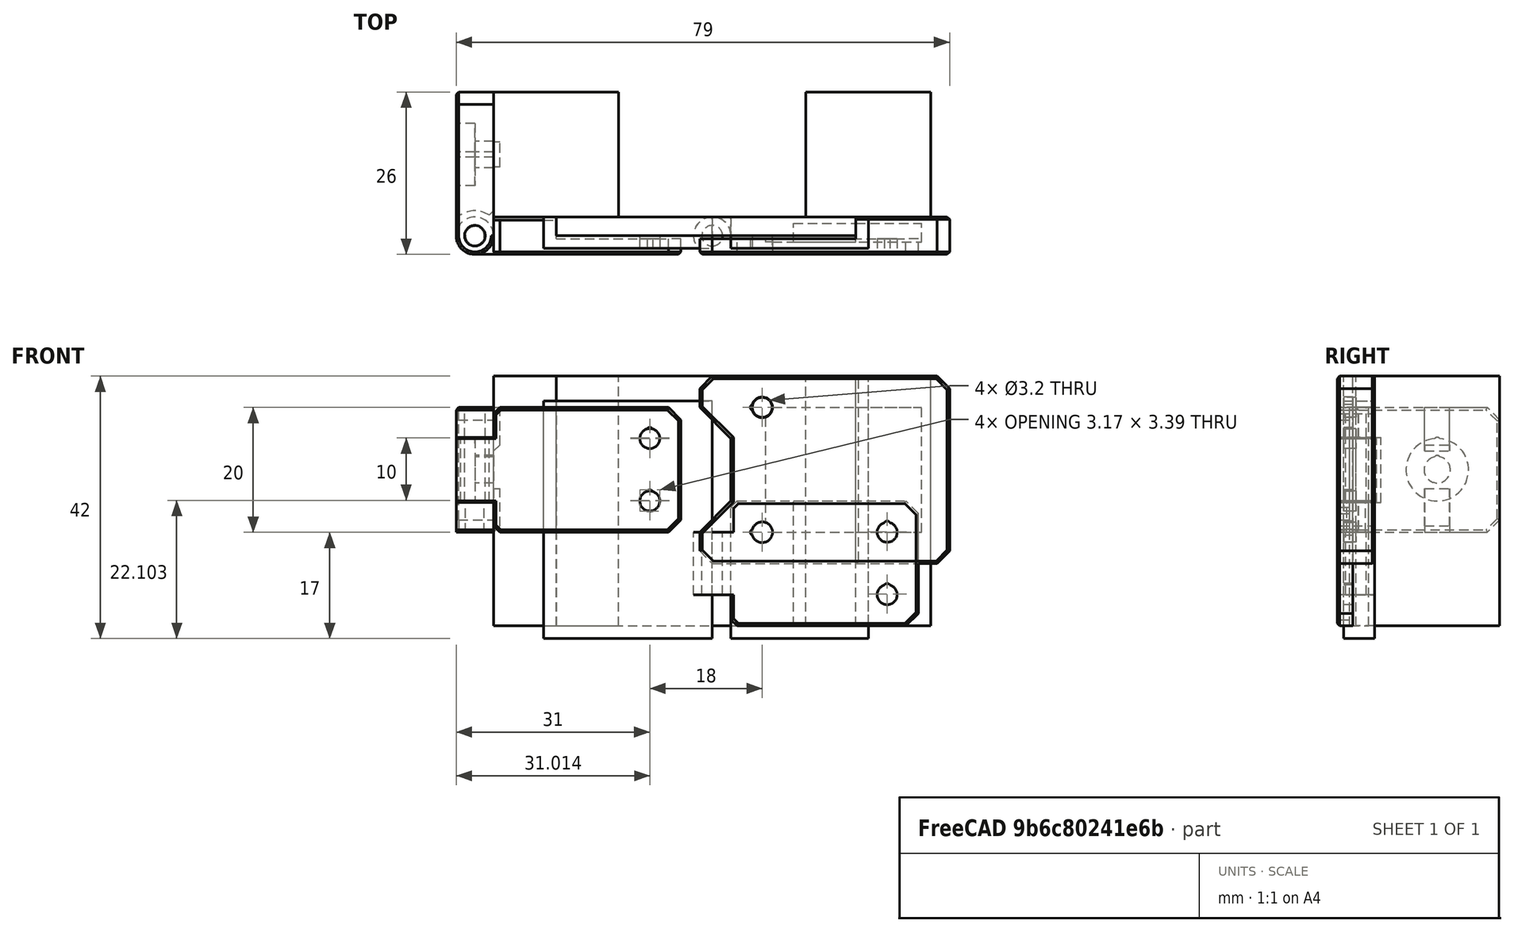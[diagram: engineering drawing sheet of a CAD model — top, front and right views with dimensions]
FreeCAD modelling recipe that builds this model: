
FCSTD DOCUMENT  (FreeCAD 0.18R14555 (Git shallow))
Label: filament-door
License: All rights reserved
LicenseURL: http://en.wikipedia.org/wiki/All_rights_reserved
objects: Part::Cylinder×27, Part::Box×20, Part::Cut×20, Part::Chamfer×14, Part::MultiFuse×13, Part::Feature×2
note: 96 computed .brp shape members not serialized (recipe doc carries the construction recipe); baked Part::Feature solids carry a one-line shape summary decoded from their .brp

FEATURE [Part::Box] Box  label="2020"
  AttacherType = Attacher::AttachEngine3D
  Height = 40
  Length = 20
  Placement = pos=(12,0,0) rot=(0,0,1;0rad)
  Width = 20
FEATURE [Part::Box] Box001  label="acrylic"
  AttacherType = Attacher::AttachEngine3D
  Height = 40
  Length = 48
  Placement = pos=(-28,-3,0) rot=(0,0,1;0rad)
  Width = 3
FEATURE [Part::Cylinder] Cylinder
  Angle = 360
  AttacherType = Attacher::AttachEngine3D
  Height = 10
  Placement = pos=(-3,-3,5) rot=(0,0,1;0rad)
  Radius = 3
FEATURE [Part::Cylinder] Cylinder001
  Angle = 360
  AttacherType = Attacher::AttachEngine3D
  Height = 10
  Placement = pos=(-3,-3,5) rot=(0,0,1;0rad)
  Radius = 1.65
FEATURE [Part::Box] Box005  label="Cube003"
  AttacherType = Attacher::AttachEngine3D
  Height = 20
  Length = 30
  Placement = pos=(0,-6,0) rot=(0,0,1;0rad)
  Width = 3
FEATURE [Part::Box] Box006  label="Cube004"
  AttacherType = Attacher::AttachEngine3D
  Height = 20
  Length = 30
  Placement = pos=(0,-3.5,0) rot=(0,0,1;0rad)
  Width = 3
FEATURE [Part::Box] Box007  label="Cube005"
  AttacherType = Attacher::AttachEngine3D
  Height = 10
  Length = 4
  Placement = pos=(-3,-6,5) rot=(0,0,1;0rad)
  Width = 3
FEATURE [Part::Cylinder] Cylinder002
  Angle = 360
  AttacherType = Attacher::AttachEngine3D
  Height = 10
  Placement = pos=(25,1.1e-15,5) rot=(1,0,0;1.5708rad)
  Radius = 0.5
FEATURE [Part::Cylinder] Cylinder003
  Angle = 360
  AttacherType = Attacher::AttachEngine3D
  Height = 10
  Placement = pos=(25,3e-15,15) rot=(1,0,0;1.5708rad)
  Radius = 0.5
FEATURE [Part::Cylinder] Cylinder004
  Angle = 360
  AttacherType = Attacher::AttachEngine3D
  Height = 10
  Placement = pos=(25,3e-15,15) rot=(1,0,0;1.5708rad)
  Radius = 1.6
FEATURE [Part::Cylinder] Cylinder005
  Angle = 360
  AttacherType = Attacher::AttachEngine3D
  Height = 10
  Placement = pos=(25,1.1e-15,5) rot=(1,0,0;1.5708rad)
  Radius = 1.6
FEATURE [Part::Chamfer] Chamfer
  Base = -> Box005
  Edges = 2 edges r=1: [Edge2,Edge4]
FEATURE [Part::Chamfer] Chamfer001
  Base = -> Chamfer
  Edges = 2 edges r=2: [Edge17,Edge18]
FEATURE [Part::Chamfer] Chamfer002
  Base = -> Chamfer001
  Edges = 8 edges r=0.4: [Edge1,Edge2,Edge3,Edge4,Edge5,Edge6,Edge7,Edge8]
FEATURE [Part::MultiFuse] Fusion
  Shapes = -> [Chamfer002,Box007,Cylinder]
FEATURE [Part::Cut] Cut
  Base = -> Fusion
  Tool = -> Box006
FEATURE [Part::Cut] Cut001
  Base = -> Cut
  Tool = -> Cylinder001
FEATURE [Part::MultiFuse] Fusion001
  Shapes = -> [Cylinder004,Cylinder005]
FEATURE [Part::Cut] Cut002
  Base = -> Cut001
  Tool = -> Fusion001
FEATURE [Part::MultiFuse] Fusion002
  Placement = pos=(0,0,1.3) rot=(0,0,1;0rad)
  Shapes = -> [Cylinder002,Cylinder003]
FEATURE [Part::Cut] Cut003  label="arm"
  Base = -> Cut002
  Placement = pos=(-38,0,15) rot=(0,0,1;0rad)
  Tool = -> Fusion002
FEATURE [Part::Cylinder] Cylinder006
  Angle = 360
  AttacherType = Attacher::AttachEngine3D
  Height = 4.8
  Placement = pos=(-3,-3,0) rot=(0,0,1;0rad)
  Radius = 3
FEATURE [Part::Cylinder] Cylinder007
  Angle = 360
  AttacherType = Attacher::AttachEngine3D
  Height = 4.8
  Placement = pos=(-3,-3,15.2) rot=(0,0,1;0rad)
  Radius = 3
FEATURE [Part::Box] Box008  label="Cube"
  AttacherType = Attacher::AttachEngine3D
  Height = 20
  Length = 6
  Placement = pos=(-6,-3,0) rot=(0,0,1;0rad)
  Width = 23
FEATURE [Part::Box] Box009  label="Cube006"
  AttacherType = Attacher::AttachEngine3D
  Height = 10.4
  Length = 6
  Placement = pos=(-6,-3,4.8) rot=(0,0,1;0rad)
  Width = 3
FEATURE [Part::Cylinder] Cylinder008
  Angle = 360
  AttacherType = Attacher::AttachEngine3D
  Height = 4.8
  Placement = pos=(-3,-3,15.2) rot=(0,0,1;0rad)
  Radius = 1.65
FEATURE [Part::Cylinder] Cylinder009
  Angle = 360
  AttacherType = Attacher::AttachEngine3D
  Height = 4.8
  Placement = pos=(-3,-3,0) rot=(0,0,1;0rad)
  Radius = 1.65
FEATURE [Part::MultiFuse] Fusion004
  Shapes = -> [Cylinder009,Cylinder008]
FEATURE [Part::Chamfer] Chamfer003
  Base = -> Box008
  Edges = 2 edges r=2: [Edge11,Edge12]
FEATURE [Part::Chamfer] Chamfer004
  Base = -> Chamfer003
  Edges = 6 edges r=0.4: [Edge1,Edge2,Edge3,Edge4,Edge5,Edge6]
FEATURE [Part::Chamfer] Chamfer005
  Base = -> Cylinder007
  Edges = 1 edges r=0.4: [Edge1]
FEATURE [Part::Chamfer] Chamfer006
  Base = -> Cylinder006
  Edges = 1 edges r=0.4: [Edge3]
FEATURE [Part::Cut] Cut004
  Base = -> Chamfer004
  Tool = -> Box009
FEATURE [Part::MultiFuse] Fusion005
  Shapes = -> [Cut004,Chamfer005,Chamfer006]
FEATURE [Part::Cut] Cut005
  Base = -> Fusion005
  Tool = -> Fusion004
FEATURE [Part::Chamfer] Chamfer007
  Base = -> Cut005
  Edges = 2 edges r=1: [Edge8,Edge28]
FEATURE [Part::Cylinder] Cylinder010
  Angle = 360
  AttacherType = Attacher::AttachEngine3D
  Height = 10
  Placement = pos=(-2e-15,10,10) rot=(0,-1,0;1.5708rad)
  Radius = 2.1
FEATURE [Part::Cylinder] Cylinder011
  Angle = 360
  AttacherType = Attacher::AttachEngine3D
  Height = 10
  Placement = pos=(-2e-15,10,11.8) rot=(0,-1,0;1.5708rad)
  Radius = 0.5
FEATURE [Part::Cut] Cut006
  Base = -> Chamfer007
  Tool = -> Cylinder010
FEATURE [Part::Cut] Cut007
  Base = -> Cut006
  Tool = -> Cylinder011
FEATURE [Part::Cylinder] Cylinder012
  Angle = 360
  AttacherType = Attacher::AttachEngine3D
  Height = 10
  Placement = pos=(-3,10,14.7) rot=(0,-1,0;1.5708rad)
  Radius = 0.5
FEATURE [Part::Cylinder] Cylinder013
  Angle = 360
  AttacherType = Attacher::AttachEngine3D
  Height = 10
  Placement = pos=(-3,10,10) rot=(0,-1,0;1.5708rad)
  Radius = 5
FEATURE [Part::Cut] Cut008
  Base = -> Cut007
  Tool = -> Cylinder013
FEATURE [Part::Cut] Cut009
  Base = -> Cut008
  Tool = -> Cylinder012
FEATURE [Part::Box] Box010  label="Cube007"
  AttacherType = Attacher::AttachEngine3D
  Height = 7
  Length = 2
  Placement = pos=(-1,8,0) rot=(0,0,1;0rad)
  Width = 4
FEATURE [Part::Box] Box011  label="Cube008"
  AttacherType = Attacher::AttachEngine3D
  Height = 7
  Length = 2
  Placement = pos=(-1,8,13) rot=(0,0,1;0rad)
  Width = 4
FEATURE [Part::Chamfer] Chamfer008
  Base = -> Box011
  Edges = 1 edges r=1: [Edge8]
FEATURE [Part::Chamfer] Chamfer009
  Base = -> Box010
  Edges = 1 edges r=1: [Edge8]
FEATURE [Part::MultiFuse] Fusion006
  Shapes = -> [Chamfer009,Cut009,Chamfer008]
FEATURE [Part::Cylinder] Cylinder014
  Angle = 360
  AttacherType = Attacher::AttachEngine3D
  Height = 4.8
  Placement = pos=(-41,-3,15) rot=(0,0,1;0rad)
  Radius = 3
FEATURE [Part::Cylinder] Cylinder015
  Angle = 360
  AttacherType = Attacher::AttachEngine3D
  Height = 10
  Placement = pos=(-41,-3,20) rot=(0,0,1;0rad)
  Radius = 3
FEATURE [Part::Cylinder] Cylinder016
  Angle = 360
  AttacherType = Attacher::AttachEngine3D
  Height = 10.4
  Placement = pos=(-3,-3,4.8) rot=(0,0,1;0rad)
  Radius = 4
FEATURE [Part::Cut] Cut010
  Base = -> Fusion006
  Tool = -> Cylinder016
FEATURE [Part::Cylinder] Cylinder017
  Angle = 360
  AttacherType = Attacher::AttachEngine3D
  Height = 4.8
  Placement = pos=(-3,-3,0) rot=(0,0,1;0rad)
  Radius = 2
FEATURE [Part::Cylinder] Cylinder018
  Angle = 360
  AttacherType = Attacher::AttachEngine3D
  Height = 4.8
  Placement = pos=(-3,-3,0) rot=(0,0,1;0rad)
  Radius = 1.5
FEATURE [Part::Cut] Cut011
  Base = -> Cylinder017
  Tool = -> Cylinder018
FEATURE [Part::MultiFuse] Fusion007  label="base"
  Placement = pos=(-38,0,15) rot=(0,0,1;0rad)
  Shapes = -> [Cut010,Cut011]
FEATURE [Part::Feature] Cut003001  label="arm001"
  shape: bbox 36 x 6 x 20 mm, 29 faces (baked)
FEATURE [Part::Feature] Fusion007001  label="base001"
  Placement = pos=(-38,0,15) rot=(0,0,1;0rad)
  shape: bbox 7 x 26 x 20 mm, 41 faces (baked)
FEATURE [Part::Box] Box012  label="Cube009"
  AttacherType = Attacher::AttachEngine3D
  Height = 38
  Length = 27
  Placement = pos=(8,0,-17) rot=(0,0,1;0rad)
  Width = 5
FEATURE [Part::Box] Box013  label="Cube010"
  AttacherType = Attacher::AttachEngine3D
  Height = 38
  Length = 32
  Placement = pos=(10,2,-15) rot=(0,0,1;0rad)
  Width = 5
FEATURE [Part::Cylinder] Cylinder019
  Angle = 360
  AttacherType = Attacher::AttachEngine3D
  Height = 10
  Placement = pos=(25,1.1e-15,5) rot=(1,0,0;1.5708rad)
  Radius = 1.6
FEATURE [Part::Cylinder] Cylinder020
  Angle = 360
  AttacherType = Attacher::AttachEngine3D
  Height = 10
  Placement = pos=(25,3e-15,15) rot=(1,0,0;1.5708rad)
  Radius = 1.6
FEATURE [Part::MultiFuse] Fusion007002
  Placement = pos=(0,5,0) rot=(0,0,1;0rad)
  Shapes = -> [Cylinder019,Cylinder020]
FEATURE [Part::Box] Box015  label="magnet"
  AttacherType = Attacher::AttachEngine3D
  Height = 20
  Length = 10
  Placement = pos=(10,-4,0) rot=(0,0,1;0rad)
  Width = 3
FEATURE [Part::Box] Box016  label="magnet001"
  AttacherType = Attacher::AttachEngine3D
  Height = 20
  Length = 25
  Placement = pos=(5.5,-4,5) rot=(0,0,1;0rad)
  Width = 3
FEATURE [Part::Box] Box021  label="2020001"
  AttacherType = Attacher::AttachEngine3D
  Height = 40
  Length = 20
  Placement = pos=(-38,0,0) rot=(0,0,1;0rad)
  Width = 20
FEATURE [Part::Box] Box022  label="Cube011"
  AttacherType = Attacher::AttachEngine3D
  Height = 30
  Length = 40
  Placement = pos=(-5,-6,0) rot=(0,0,1;0rad)
  Width = 6
FEATURE [Part::Box] Box023  label="Cube012"
  AttacherType = Attacher::AttachEngine3D
  Height = 30
  Length = 25
  Placement = pos=(-5,-3.5,0) rot=(0,0,1;0rad)
  Width = 3.5
FEATURE [Part::Cut] Cut003004
  Base = -> Box022
  Tool = -> Box023
FEATURE [Part::Cylinder] Cylinder021
  Angle = 360
  AttacherType = Attacher::AttachEngine3D
  Height = 10
  Placement = pos=(5,-1e-15,5) rot=(1,0,0;1.5708rad)
  Radius = 0.5
FEATURE [Part::Cylinder] Cylinder022
  Angle = 360
  AttacherType = Attacher::AttachEngine3D
  Height = 10
  Placement = pos=(5,3e-15,25) rot=(1,0,0;1.5708rad)
  Radius = 0.5
FEATURE [Part::Cylinder] Cylinder023
  Angle = 360
  AttacherType = Attacher::AttachEngine3D
  Height = 10
  Placement = pos=(5,-1e-15,5) rot=(1,0,0;1.5708rad)
  Radius = 1.65
FEATURE [Part::Cylinder] Cylinder024
  Angle = 360
  AttacherType = Attacher::AttachEngine3D
  Height = 10
  Placement = pos=(5,3e-15,25) rot=(1,0,0;1.5708rad)
  Radius = 1.65
FEATURE [Part::MultiFuse] Fusion007003
  Shapes = -> [Cylinder024,Cylinder023]
FEATURE [Part::MultiFuse] Fusion007004
  Placement = pos=(-1.4,0,0) rot=(0,0,1;0rad)
  Shapes = -> [Cylinder021,Cylinder022]
FEATURE [Part::MultiFuse] Fusion007005
  Shapes = -> [Fusion007003,Fusion007004]
FEATURE [Part::Cut] Cut003005
  Base = -> Cut003004
  Tool = -> Box016
FEATURE [Part::Chamfer] Chamfer010
  Base = -> Cut003005
  Edges = 4 edges r=2: [Edge1,Edge3,Edge8,Edge18]
FEATURE [Part::Box] Box024  label="Cube013"
  AttacherType = Attacher::AttachEngine3D
  Height = 20
  Length = 10
  Placement = pos=(-10,-11,0) rot=(0,0,1;0rad)
  Width = 10
FEATURE [Part::Chamfer] Chamfer011
  Base = -> Box024
  Edges = 2 edges r=5: [Edge6,Edge8]
  Placement = pos=(0,0,5) rot=(0,0,1;0rad)
FEATURE [Part::Cut] Cut003006
  Base = -> Chamfer010
  Tool = -> Chamfer011
FEATURE [Part::Chamfer] Chamfer012
  Base = -> Cut003006
  Edges = 18 edges r=0.4: [Edge2,Edge5,Edge8,Edge9,Edge10,Edge11,Edge12,Edge13,Edge14,Edge15,Edge16,Edge17,Edge32,Edge35,Edge37,Edge39,Edge42,Edge49]
FEATURE [Part::Cut] Cut003007  label="handle"
  Base = -> Chamfer012
  Placement = pos=(0,0,10) rot=(0,0,1;0rad)
  Tool = -> Fusion007005
FEATURE [Part::Box] Box025  label="Cube014"
  AttacherType = Attacher::AttachEngine3D
  Height = 42
  Length = 22
  Placement = pos=(0,-5,-2) rot=(0,0,1;0rad)
  Width = 5
FEATURE [Part::Box] Box026  label="Cube015"
  AttacherType = Attacher::AttachEngine3D
  Height = 42
  Length = 22
  Placement = pos=(-2,-3,0) rot=(0,0,1;0rad)
  Width = 5
FEATURE [Part::Cylinder] Cylinder025
  Angle = 360
  AttacherType = Attacher::AttachEngine3D
  Height = 10
  Placement = pos=(5,2.2e-15,10) rot=(1,0,0;1.5708rad)
  Radius = 1.6
FEATURE [Part::Cylinder] Cylinder026
  Angle = 360
  AttacherType = Attacher::AttachEngine3D
  Height = 10
  Placement = pos=(5,7e-15,30) rot=(1,0,0;1.5708rad)
  Radius = 1.6
FEATURE [Part::MultiFuse] Fusion007006
  Placement = pos=(0,0,5) rot=(0,0,1;0rad)
  Shapes = -> [Cylinder026,Cylinder025]
FEATURE [Part::Cut] Cut003010
  Base = -> Box012
  Tool = -> Box013
FEATURE [Part::Cut] Cut003011  label="hingle-drill-template"
  Base = -> Cut003010
  Placement = pos=(-38,-5,15) rot=(0,0,1;0rad)
  Tool = -> Fusion007002
FEATURE [Part::Box] Box027  label="Cube016"
  AttacherType = Attacher::AttachEngine3D
  Height = 20
  Length = 10
  Placement = pos=(-38,-3.5,15) rot=(0,0,1;0rad)
  Width = 3
FEATURE [Part::Chamfer] Chamfer013
  Base = -> Box027
  Edges = 2 edges r=1: [Edge2,Edge4]
FEATURE [Part::MultiFuse] Fusion007007  label="arm-r2"
  Shapes = -> [Cut003,Chamfer013]
FEATURE [Part::Cut] Cut003012
  Base = -> Box025
  Tool = -> Box026
FEATURE [Part::Cut] Cut003013
  Base = -> Cut003012
  Tool = -> Fusion007006
